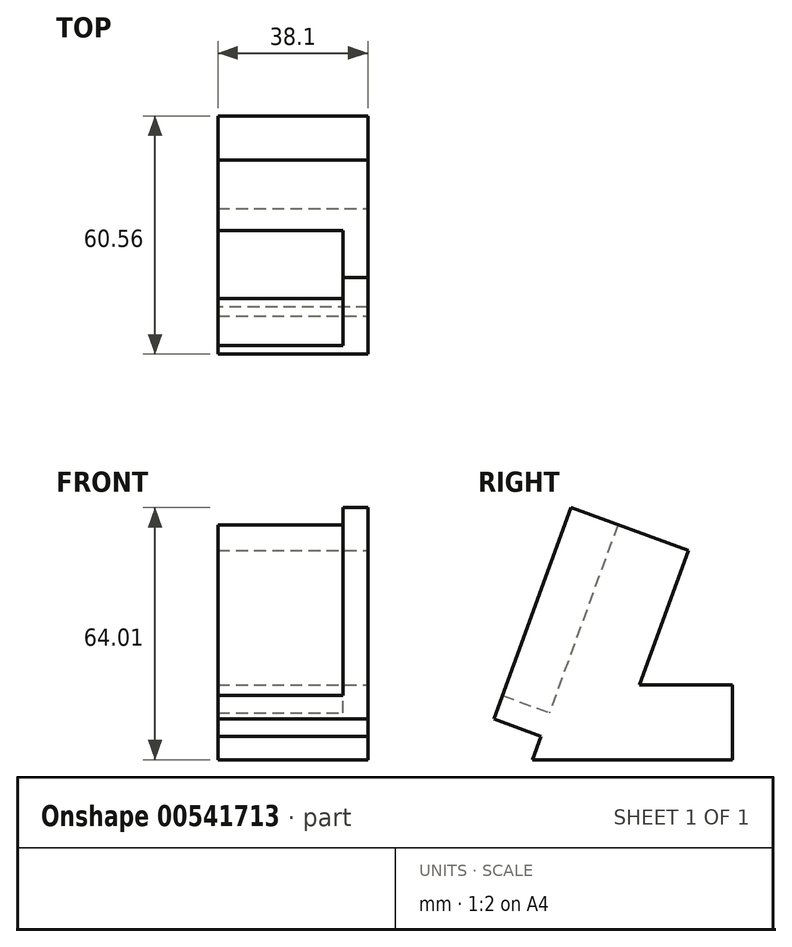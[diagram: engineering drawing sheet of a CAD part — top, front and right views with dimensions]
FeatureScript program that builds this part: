
annotation { "Feature Type Name" : "Feature", "Feature Type Description" : "" }
export const myFeature = defineFeature(function(context is Context, id is Id, definition is map)
    precondition{}
    {
        {
            var Q0;
            Q0=qCreatedBy(makeId("Right.planeOp"),FACE);
            var sketch = newSketch(context, id + "F0", { "sketchPlane" : qUnion([Q0])});
            skLineSegment(sketch, "E0", {"start": v(0, 0) * mm, "end": v(50.8, 0) * mm});
            skLineSegment(sketch, "E1", {"start": v(50.8, 0) * mm, "end": v(50.8, 19.05) * mm});
            skLineSegment(sketch, "E2", {"start": v(50.8, 19.05) * mm, "end": v(27.2, 19.05) * mm});
            skLineSegment(sketch, "E3", {"start": v(27.2, 19.05) * mm, "end": v(39.62, 53.15) * mm});
            skLineSegment(sketch, "E4", {"start": v(39.62, 53.15) * mm, "end": v(21.72, 59.67) * mm});
            skLineSegment(sketch, "E5", {"start": v(21.72, 59.67) * mm, "end": v(0, 0) * mm});
            skSolve(sketch);
        }
        {
            var Q0;
            Q0=makeQuery(id+"F0.imprint","IMPRINT",FACE,{"disambiguationData":[TD([[makeQuery(id+"F0.imprint","IMPRINT",EDGE,{"derivedFrom":sQuery(id+"F0.wireOp",EDGE,"E0")}),1.0]])]});
            extrude(context, id + "F1", {"entities" : qUnion([Q0]), "oppositeDirection" : true, "depth" : 38.1 * mm, "offsetDistance" : 25.4 * mm});
        }
        {
            var Q0;
            Q0=makeQuery(id+"F1.opExtrude","SWEPT_FACE",FACE,{"disambiguationData":[OSD([sQuery(id+"F0.wireOp",EDGE,"E5")])]});
            var sketch = newSketch(context, id + "F2", { "sketchPlane" : qUnion([Q0])});
            skLineSegment(sketch, "E6", {"start": v(0, 63.5) * mm, "end": v(0, 6.35) * mm});
            skLineSegment(sketch, "E7", {"start": v(0, 6.35) * mm, "end": v(-38.1, 6.35) * mm});
            skLineSegment(sketch, "E8", {"start": v(-38.1, 6.35) * mm, "end": v(-38.1, 12.7) * mm});
            skLineSegment(sketch, "E9", {"start": v(-38.1, 12.7) * mm, "end": v(-6.35, 12.7) * mm});
            skLineSegment(sketch, "E10", {"start": v(-6.35, 12.7) * mm, "end": v(-6.35, 63.5) * mm});
            skLineSegment(sketch, "E11", {"start": v(-6.35, 63.5) * mm, "end": v(0, 63.5) * mm});
            skSolve(sketch);
        }
        {
            var Q0;
            Q0=makeQuery(id+"F2.imprint","IMPRINT",FACE,{"disambiguationData":[TD([[makeQuery(id+"F2.imprint","IMPRINT",EDGE,{"derivedFrom":sQuery(id+"F2.wireOp",EDGE,"E6")}),-1.0]])]});
            extrude(context, id + "F3", {"entities" : qUnion([Q0]), "operationType" : NewBodyOperationType.ADD, "depth" : 12.7 * mm, "offsetDistance" : 25.4 * mm});
        }
    });
